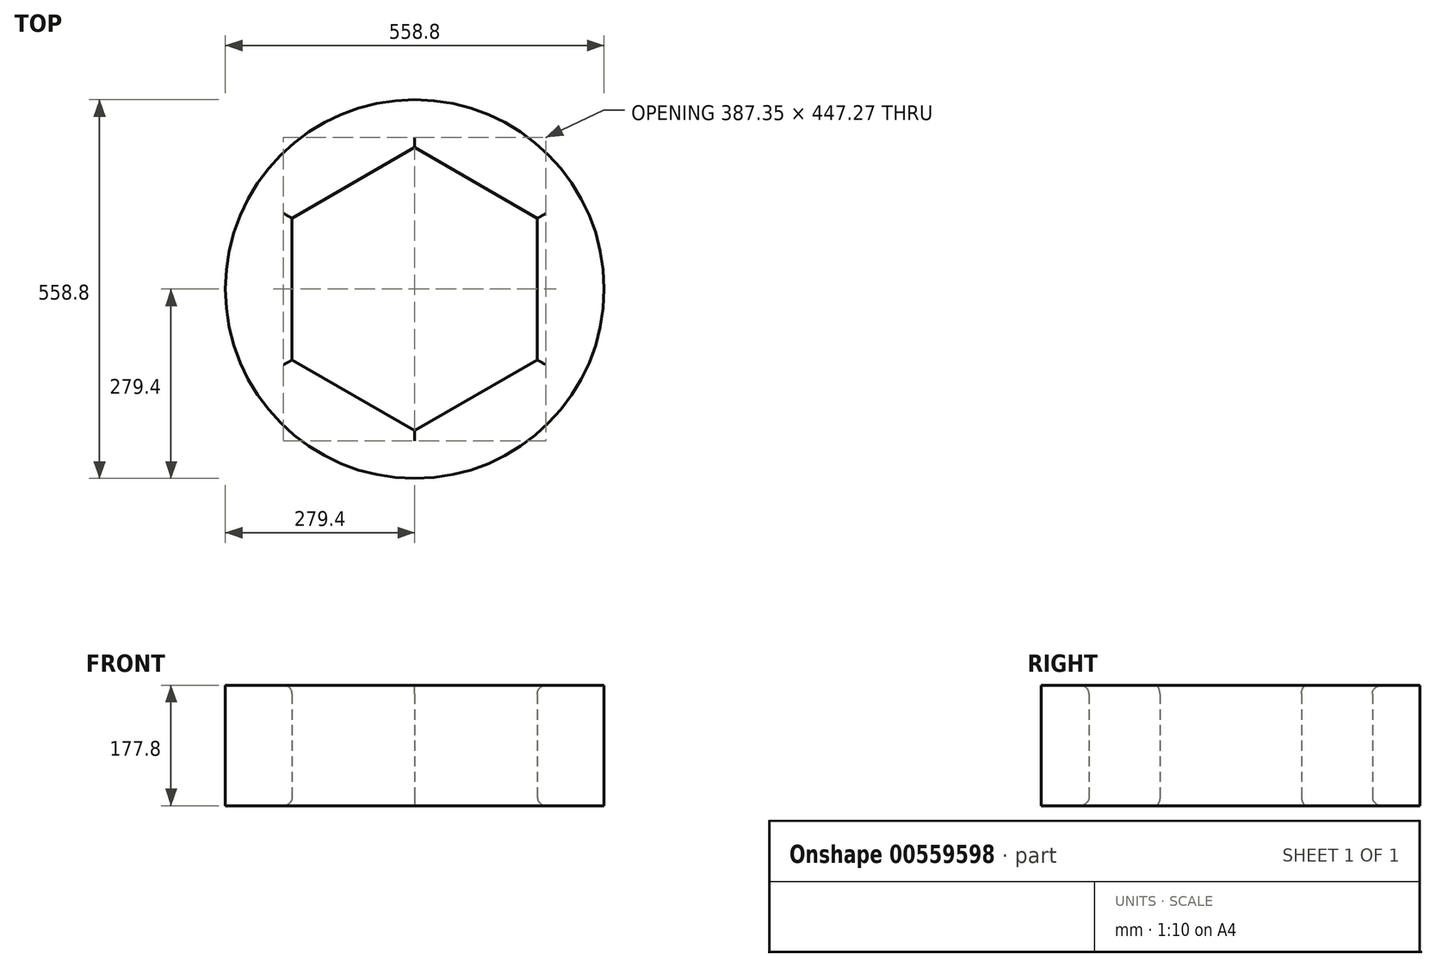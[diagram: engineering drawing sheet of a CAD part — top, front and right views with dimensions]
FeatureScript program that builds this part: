
annotation { "Feature Type Name" : "Feature", "Feature Type Description" : "" }
export const myFeature = defineFeature(function(context is Context, id is Id, definition is map)
    precondition{}
    {
        {
            var Q0;
            Q0=qCreatedBy(makeId("Top.planeOp"),FACE);
            var sketch = newSketch(context, id + "F0", { "sketchPlane" : qUnion([Q0])});
            skCircle(sketch, "E0", {"center": v(0, 0) * mm, "radius": 279.4 * mm});
            skCircle(sketch, "E1.cCircle", {"center": v(0, 0) * mm, "radius": 180.98 * mm, "construction": true});
            skLineSegment(sketch, "E1.0", {"start": v(180.98, 104.49) * mm, "end": v(180.98, -104.49) * mm});
            skLineSegment(sketch, "E1.1", {"start": v(180.97, -104.49) * mm, "end": v(0, -208.97) * mm});
            skLineSegment(sketch, "E1.2", {"start": v(0, -208.97) * mm, "end": v(-180.97, -104.49) * mm});
            skLineSegment(sketch, "E1.3", {"start": v(-180.97, -104.49) * mm, "end": v(-180.98, 104.49) * mm});
            skLineSegment(sketch, "E1.4", {"start": v(-180.98, 104.49) * mm, "end": v(0, 208.97) * mm});
            skLineSegment(sketch, "E1.5", {"start": v(0, 208.97) * mm, "end": v(180.97, 104.49) * mm});
            skPoint(sketch, "E1.0.midPoint", {"position": v(180.98, 0) * mm});
            skSolve(sketch);
        }
        {
            var Q0;
            Q0=makeQuery(id+"F0.imprint","IMPRINT",FACE,{"disambiguationData":[TD([[makeQuery(id+"F0.imprint","IMPRINT",EDGE,{"derivedFrom":sQuery(id+"F0.wireOp",EDGE,"E0")}),1.0]])]});
            extrude(context, id + "F1", {"entities" : qUnion([Q0]), "depth" : 177.8 * mm, "offsetDistance" : 25.4 * mm});
        }
        {
            var Q0;
            Q0=makeQuery(id+"F1.opExtrude","CAP_EDGE",EDGE,{"disambiguationData":[OSD([sQuery(id+"F0.wireOp",EDGE,"E1.4")])],"isStart":false});
            var Q1;
            Q1=makeQuery(id+"F1.opExtrude","CAP_EDGE",EDGE,{"disambiguationData":[OSD([sQuery(id+"F0.wireOp",EDGE,"E1.5")])],"isStart":false});
            var Q2;
            Q2=makeQuery(id+"F1.opExtrude","CAP_EDGE",EDGE,{"disambiguationData":[OSD([sQuery(id+"F0.wireOp",EDGE,"E1.3")])],"isStart":false});
            var Q3;
            Q3=makeQuery(id+"F1.opExtrude","CAP_EDGE",EDGE,{"disambiguationData":[OSD([sQuery(id+"F0.wireOp",EDGE,"E1.2")])],"isStart":false});
            var Q4;
            Q4=makeQuery(id+"F1.opExtrude","CAP_EDGE",EDGE,{"disambiguationData":[OSD([sQuery(id+"F0.wireOp",EDGE,"E1.1")])],"isStart":false});
            var Q5;
            Q5=makeQuery(id+"F1.opExtrude","CAP_EDGE",EDGE,{"disambiguationData":[OSD([sQuery(id+"F0.wireOp",EDGE,"E1.0")])],"isStart":false});
            fillet(context, id + "F2", {"entities" : qUnion([Q0, Q1, Q2, Q3, Q4, Q5]), "radius" : 12.7 * mm, "tangentPropagation" : true, "allowEdgeOverflow" : false});
        }
        {
            var Q0;
            Q0=makeQuery(id+"F1.opExtrude","CAP_EDGE",EDGE,{"disambiguationData":[OSD([sQuery(id+"F0.wireOp",EDGE,"E1.3")])],"isStart":true});
            var Q1;
            Q1=makeQuery(id+"F1.opExtrude","CAP_EDGE",EDGE,{"disambiguationData":[OSD([sQuery(id+"F0.wireOp",EDGE,"E1.2")])],"isStart":true});
            var Q2;
            Q2=makeQuery(id+"F1.opExtrude","CAP_EDGE",EDGE,{"disambiguationData":[OSD([sQuery(id+"F0.wireOp",EDGE,"E1.1")])],"isStart":true});
            var Q3;
            Q3=makeQuery(id+"F1.opExtrude","CAP_EDGE",EDGE,{"disambiguationData":[OSD([sQuery(id+"F0.wireOp",EDGE,"E1.0")])],"isStart":true});
            var Q4;
            Q4=makeQuery(id+"F1.opExtrude","CAP_EDGE",EDGE,{"disambiguationData":[OSD([sQuery(id+"F0.wireOp",EDGE,"E1.5")])],"isStart":true});
            var Q5;
            Q5=makeQuery(id+"F1.opExtrude","CAP_EDGE",EDGE,{"disambiguationData":[OSD([sQuery(id+"F0.wireOp",EDGE,"E1.4")])],"isStart":true});
            fillet(context, id + "F3", {"entities" : qUnion([Q0, Q1, Q2, Q3, Q4, Q5]), "radius" : 12.7 * mm, "tangentPropagation" : true, "allowEdgeOverflow" : false});
        }
    });
